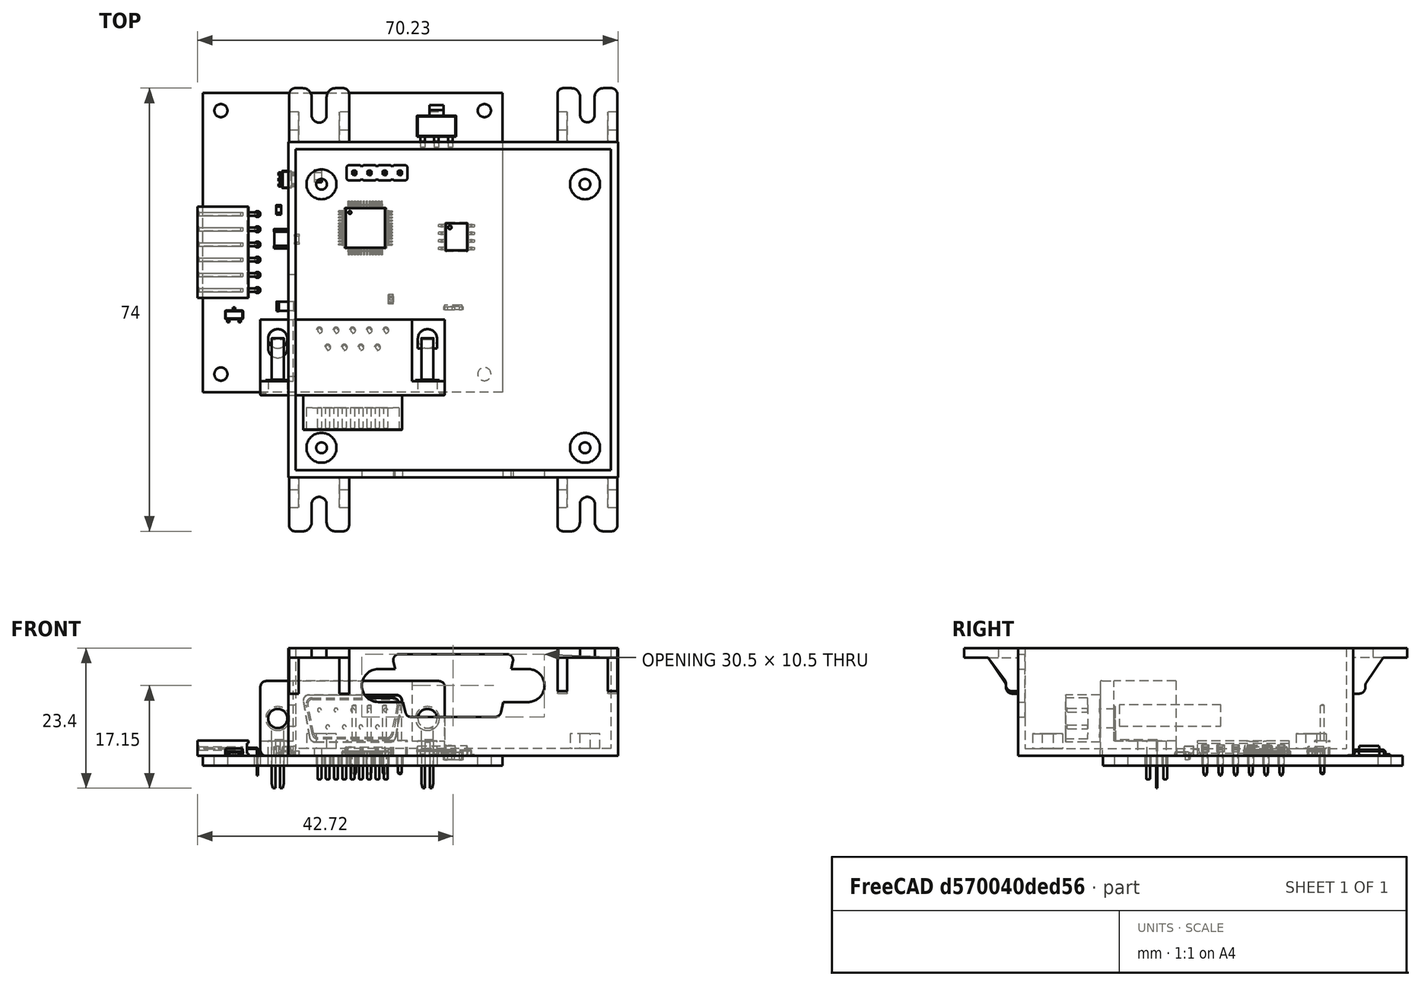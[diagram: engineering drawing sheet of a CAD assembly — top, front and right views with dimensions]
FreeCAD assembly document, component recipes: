
FREECAD ASSEMBLY — COMPONENT RECIPES ("CentralBox_Stuffed")

This assembly document has 6 components, labeled P0..P5 below (a component is one placed body or linked part). 5 of them carry a construction recipe — the FreeCAD feature program that regenerates the part from scratch, quoted from this document or its linked companion documents; the rest are supplied as boundary geometry only. No exploded tour is included for this assembly.
COMPONENT P0 — geometry summary ("CTB-01.kicad_pro"; no construction recipe available for this part):
  bounding box: 56.3 x 50.9 x 17.9 mm
  tessellated surface: 83,718 triangles
  volume: 7836 mm^3 (15% of its bounding box)
COMPONENT P1 — recipe-attached ("Body", modeled in this document).
Construction recipe (the document's own serialized feature program — sketch geometry with constraints, then the solid features built on it; lengths are millimeters unless a unit is written):

FEATURE [Sketcher::SketchObject] Sketch
  FullyConstrained = true
  MapMode = 2
  Support = -> [XY_Plane]
  expr: Constraints[8] = <<Params>>.box_width_external
  expr: Constraints[9] = <<Params>>.box_length_external
  sketch-geometry (4):
    g0: LineSegment StartX=-27.5 StartY=28 StartZ=0 EndX=27.5 EndY=28 EndZ=0
    g1: LineSegment StartX=27.5 StartY=28 StartZ=0 EndX=27.5 EndY=-28 EndZ=0
    g2: LineSegment StartX=27.5 StartY=-28 StartZ=0 EndX=-27.5 EndY=-28 EndZ=0
    g3: LineSegment StartX=-27.5 StartY=-28 StartZ=0 EndX=-27.5 EndY=28 EndZ=0
  constraints (10):
    c: Coincident(g0,g1)
    c: Coincident(g1,g2)
    c: Coincident(g2,g3)
    c: Coincident(g3,g0)
    c: Horizontal(g2)
    c: Vertical(g3)
    c: Symmetric(g0,g1,g-1)
    c: Symmetric(g0,g0,g-2)
    c: DistanceY(g2,g0) = 56
    c: DistanceX(g0,g0) = 55
FEATURE [PartDesign::Pad] Pad
  Direction = (0,0,1)
  Length = 18
  Length2 = 10
  Profile = -> Sketch
  ReferenceAxis = -> Sketch [N_Axis]
  Type = 0
  expr: Length = <<Params>>.box_height
FEATURE [Sketcher::SketchObject] Sketch012
  FullyConstrained = true
  MapMode = 5
  Placement = pos=(0,0,18) rot=(0,0,1;0rad)
  Support = -> [Pad]
  expr: Constraints[8] = <<Params>>.box_length_internal
  expr: Constraints[9] = <<Params>>.box_width_internal
  sketch-geometry (4):
    g0: LineSegment StartX=-26.3 StartY=26.8 StartZ=0 EndX=26.3 EndY=26.8 EndZ=0
    g1: LineSegment StartX=26.3 StartY=26.8 StartZ=0 EndX=26.3 EndY=-26.8 EndZ=0
    g2: LineSegment StartX=26.3 StartY=-26.8 StartZ=0 EndX=-26.3 EndY=-26.8 EndZ=0
    g3: LineSegment StartX=-26.3 StartY=-26.8 StartZ=0 EndX=-26.3 EndY=26.8 EndZ=0
  constraints (10):
    c: Coincident(g0,g1)
    c: Coincident(g1,g2)
    c: Coincident(g2,g3)
    c: Coincident(g3,g0)
    c: Horizontal(g2)
    c: Vertical(g1)
    c: Symmetric(g0,g0,g-2)
    c: Symmetric(g0,g2,g-1)
    c: DistanceX(g0,g0) = 52.6
    c: DistanceY(g2,g0) = 53.6
FEATURE [PartDesign::Pocket] Pocket
  BaseFeature = -> Pad
  Direction = (0,0,-1)
  Length = 16.8
  Length2 = 5
  Profile = -> Sketch012
  ReferenceAxis = -> Sketch012 [N_Axis]
  Type = 0
  expr: Length = <<Params>>.box_depth
FEATURE [PartDesign::SubShapeBinder] Binder
  BindCopyOnChange = 0
  BindMode = 0
  ClaimChildren = false
  Context = -> Body [Binder.]
  Fuse = false
  MakeFace = true
  OffsetFill = false
  OffsetIntersection = false
  OffsetJoinType = 0
  OffsetOpenResult = false
  PartialLoad = false
  Relative = true
  Support = -> [Board_1da8[Step_Models_1da8.Top_1da8.Shape011.Face27]]
  _Version = 2
FEATURE [Sketcher::SketchObject] Sketch013
  ExternalGeometry = -> [Binder]
  FullyConstrained = true
  MapMode = 5
  Placement = pos=(0,-28,0) rot=(1,0,0;1.5708rad)
  Support = -> [Pocket]
  sketch-geometry (17):
    g0: ArcOfCircle CenterX=12.49 CenterY=11.75 CenterZ=0 NormalX=0 NormalY=0 NormalZ=1 AngleXU=0 Radius=2.75 StartAngle=4.70512 EndAngle=7.85398
    g1: ArcOfCircle CenterX=-12.51 CenterY=11.75 CenterZ=0 NormalX=0 NormalY=0 NormalZ=1 AngleXU=0 Radius=2.75 StartAngle=1.5708 EndAngle=4.71239
    g2: LineSegment StartX=-12.51 StartY=9 StartZ=0 EndX=-8.39 EndY=9 EndZ=0
    g3: LineSegment StartX=-12.51 StartY=14.5 StartZ=0 EndX=-9.68 EndY=14.5 EndZ=0
    g4: LineSegment StartX=-12.51 StartY=11.75 StartZ=0 EndX=12.49 EndY=11.75 EndZ=0
    g5: ArcOfCircle CenterX=-9.01 CenterY=16 CenterZ=0 NormalX=0 NormalY=0 NormalZ=1 AngleXU=0 Radius=1 StartAngle=1.5708 EndAngle=3.37594
    g6: ArcOfCircle CenterX=8.99 CenterY=16 CenterZ=0 NormalX=0 NormalY=0 NormalZ=1 AngleXU=0 Radius=1 StartAngle=6.04884 EndAngle=7.85398
    g7: ArcOfCircle CenterX=6.99 CenterY=7.5 CenterZ=0 NormalX=0 NormalY=0 NormalZ=1 AngleXU=0 Radius=1 StartAngle=4.71239 EndAngle=6.06326
    g8: ArcOfCircle CenterX=-7.01 CenterY=7.5 CenterZ=0 NormalX=0 NormalY=0 NormalZ=1 AngleXU=0 Radius=1 StartAngle=3.37255 EndAngle=4.71239
    g9: LineSegment StartX=-9.01 StartY=17 StartZ=0 EndX=8.99 EndY=17 EndZ=0
    g10: LineSegment StartX=6.99 StartY=6.5 StartZ=0 EndX=-7.01 EndY=6.5 EndZ=0
    g11: LineSegment StartX=-7.98345 StartY=7.27109 StartZ=0 EndX=-8.39 EndY=9 EndZ=0
    g12: LineSegment StartX=7.96591 StartY=7.28184 StartZ=0 EndX=8.35 EndY=9 EndZ=0
    g13: LineSegment StartX=9.66 StartY=14.5 StartZ=0 EndX=12.49 EndY=14.5 EndZ=0
    g14: LineSegment StartX=-9.68 StartY=14.5 StartZ=0 EndX=-9.98267 EndY=15.7678 EndZ=0
    g15: LineSegment StartX=8.35 StartY=9 StartZ=0 EndX=12.47 EndY=9.00007 EndZ=0
    g16: LineSegment StartX=9.66 StartY=14.5 StartZ=0 EndX=9.96267 EndY=15.7678 EndZ=0
  constraints (44):
    c: Coincident(g0,g-4)
    c: Coincident(g1,g-3)
    c: Diameter(g1) = 5.5
    c: Equal(g1,g0)
    c: Coincident(g4,g1)
    c: Coincident(g4,g0)
    c: Diameter(g6) = 2
    c: Equal(g6,g5)
    c: Equal(g5,g8)
    c: Equal(g8,g7)
    c: Horizontal(g9)
    c: Horizontal(g10)
    c: DistanceY(g10,g9) = 10.5
    c: DistanceX(g5,g6) = 18
    c: DistanceX(g8,g7) = 14
    c: DistanceX(g7,g0) = 5.5
    c: DistanceY(g7,g0) = 4.25
    c: DistanceX(g6,g0) = 3.5
    c: Tangent(g5,g9) = 1.5708
    c: Tangent(g6,g9) = 1.5708
    c: Tangent(g7,g12) = -1.5708
    c: Tangent(g7,g10) = 1.5708
    c: Tangent(g8,g10) = 1.5708
    c: Tangent(g8,g11) = 1.5708
    c: Tangent(g1,g3) = 1.5708
    c: Tangent(g1,g2) = -1.5708
    c: Coincident(g0,g15) = -1.5708
    c: Coincident(g0,g13) = 1.5708
    c: Coincident(g14,g3)
    c: Coincident(g2,g11)
    c: Coincident(g16,g13)
    c: Coincident(g12,g15)
    c: Horizontal(g2,g12)
    c: Horizontal(g3,g13)
    c: Equal(g13,g3)
    c: Equal(g2,g15)
    c: DistanceX(g2,g2) = 4.12
    c: DistanceX(g1,g3) = 2.83
    c: DistanceY(g1,g3) = 2.75
    c: DistanceY(g2,g1) = 2.75
    c: DistanceX(g13,g0) = 2.83
    c: DistanceX(g12,g0) = 4.14
    c: Tangent(g5,g14) = 1.5708
    c: Tangent(g6,g16) = -1.5708
FEATURE [PartDesign::Pocket] Pocket001
  BaseFeature = -> Pocket
  Direction = (0,1,-2e-16)
  Length = 5
  Length2 = 5
  Profile = -> Sketch013
  ReferenceAxis = -> Sketch013 [N_Axis]
  Type = 2
FEATURE [Sketcher::SketchObject] Sketch014
  FullyConstrained = true
  MapMode = 5
  Placement = pos=(-27.5,0,0) rot=(0.57735,-0.57735,-0.57735;2.0944rad)
  Support = -> [Pocket001]
  expr: Constraints[10] = <<Params>>.side_window_height
  expr: Constraints[11] = <<Params>>.side_window_y
  expr: Constraints[8] = <<Params>>.side_window_length
  expr: Constraints[9] = <<Params>>.side_window_z
  sketch-geometry (4):
    g0: LineSegment StartX=-5.9 StartY=8.5 StartZ=0 EndX=11.1 EndY=8.5 EndZ=0
    g1: LineSegment StartX=11.1 StartY=8.5 StartZ=0 EndX=11.1 EndY=5 EndZ=0
    g2: LineSegment StartX=11.1 StartY=5 StartZ=0 EndX=-5.9 EndY=5 EndZ=0
    g3: LineSegment StartX=-5.9 StartY=5 StartZ=0 EndX=-5.9 EndY=8.5 EndZ=0
  constraints (12):
    c: Coincident(g0,g1)
    c: Coincident(g1,g2)
    c: Coincident(g2,g3)
    c: Coincident(g3,g0)
    c: Horizontal(g0)
    c: Horizontal(g2)
    c: Vertical(g1)
    c: Vertical(g3)
    c: DistanceX(g2,g1) = 17
    c: DistanceY(g-1,g2) = 5
    c: DistanceY(g2,g0) = 3.5
    c: DistanceX(g-1,g1) = 11.1
FEATURE [PartDesign::Pocket] Pocket002
  BaseFeature = -> Pocket001
  Direction = (1,0,0)
  Length = 5
  Length2 = 5
  Profile = -> Sketch014
  ReferenceAxis = -> Sketch014 [N_Axis]
  Type = 2
FEATURE [PartDesign::SubShapeBinder] Binder001
  BindCopyOnChange = 0
  BindMode = 0
  ClaimChildren = false
  Context = -> Body [Binder001.]
  Fuse = false
  MakeFace = true
  OffsetFill = false
  OffsetIntersection = false
  OffsetJoinType = 0
  OffsetOpenResult = false
  PartialLoad = false
  Relative = true
  Support = -> [Board_1da8[Board_Geoms_1da8.Pcb_1da8.]]
  _Version = 2
FEATURE [Sketcher::SketchObject] Sketch015
  ExternalGeometry = -> [Binder001]
  FullyConstrained = true
  MapMode = 5
  Placement = pos=(0,0,1.2) rot=(0,0,1;0rad)
  Support = -> [Pocket002]
  expr: Constraints[8] = <<Params>>.monting_boss_hole
  expr: Constraints[9] = <<Params>>.mounting_boss_pad
  sketch-geometry (8):
    g0: Circle CenterX=22 CenterY=-23.05 CenterZ=0 NormalX=0 NormalY=0 NormalZ=1 AngleXU=0 Radius=0.9
    g1: Circle CenterX=22 CenterY=-23.05 CenterZ=0 NormalX=0 NormalY=0 NormalZ=1 AngleXU=0 Radius=2.5
    g2: Circle CenterX=-22 CenterY=-23.05 CenterZ=0 NormalX=0 NormalY=0 NormalZ=1 AngleXU=0 Radius=0.9
    g3: Circle CenterX=-22 CenterY=-23.05 CenterZ=0 NormalX=0 NormalY=0 NormalZ=1 AngleXU=0 Radius=2.5
    g4: Circle CenterX=22 CenterY=20.95 CenterZ=0 NormalX=0 NormalY=0 NormalZ=1 AngleXU=0 Radius=0.9
    g5: Circle CenterX=22 CenterY=20.95 CenterZ=0 NormalX=0 NormalY=0 NormalZ=1 AngleXU=0 Radius=2.5
    g6: Circle CenterX=-22 CenterY=20.95 CenterZ=0 NormalX=0 NormalY=0 NormalZ=1 AngleXU=0 Radius=0.9
    g7: Circle CenterX=-22 CenterY=20.95 CenterZ=0 NormalX=0 NormalY=0 NormalZ=1 AngleXU=0 Radius=2.5
  constraints (16):
    c: Coincident(g0,g-5)
    c: Coincident(g1,g0)
    c: Coincident(g2,g-6)
    c: Coincident(g3,g2)
    c: Coincident(g4,g-4)
    c: Coincident(g5,g4)
    c: Coincident(g6,g-3)
    c: Coincident(g7,g6)
    c: Diameter(g4) = 1.8
    c: Diameter(g5) = 5
    c: Equal(g4,g2)
    c: Equal(g2,g0)
    c: Equal(g4,g6)
    c: Equal(g5,g7)
    c: Equal(g7,g1)
    c: Equal(g1,g3)
FEATURE [PartDesign::Pad] Pad010
  BaseFeature = -> Pocket002
  Direction = (0,0,1)
  Length = 2.5
  Length2 = 10
  Profile = -> Sketch015
  ReferenceAxis = -> Sketch015 [N_Axis]
  Type = 0
  expr: Length = <<Params>>.mounting_boss_height
FEATURE [PartDesign::Body] Body
  Group = -> [Sketch,Pad,Sketch012,Pocket,Binder,Sketch013,Pocket001,Sketch014,Pocket002,Binder001,Sketch015,Pad010]
  Origin = -> Origin
  Tip = -> Pad010
COMPONENT P2 — recipe-attached ("Tab1", modeled in this document).
Construction recipe (the document's own serialized feature program — sketch geometry with constraints, then the solid features built on it; lengths are millimeters unless a unit is written):

FEATURE [Sketcher::SketchObject] Sketch004
  FullyConstrained = true
  MapMode = 5
  Support = -> [XY_Plane009]
  expr: Constraints[13] = <<Params001>>.tab_length
  expr: Constraints[14] = <<Params001>>.tab_width
  expr: Constraints[19] = <<Params001>>.tab_hole_diameter
  expr: Constraints[20] = <<Params001>>.tab_hole_x
  sketch-geometry (8):
    g0: LineSegment StartX=-4.5 StartY=5 StartZ=0 EndX=4.5 EndY=5 EndZ=0
    g1: LineSegment StartX=4.5 StartY=5 StartZ=0 EndX=4.5 EndY=1.25 EndZ=0
    g2: LineSegment StartX=4.5 StartY=-5 StartZ=0 EndX=-4.5 EndY=-5 EndZ=0
    g3: LineSegment StartX=-4.5 StartY=-5 StartZ=0 EndX=-4.5 EndY=5 EndZ=0
    g4: ArcOfCircle CenterX=-1e-16 CenterY=0 CenterZ=0 NormalX=0 NormalY=0 NormalZ=1 AngleXU=0 Radius=1.25 StartAngle=1.5708 EndAngle=4.71239
    g5: LineSegment StartX=-3e-16 StartY=1.25 StartZ=0 EndX=4.5 EndY=1.25 EndZ=0
    g6: LineSegment StartX=4.5 StartY=-1.25 StartZ=0 EndX=0 EndY=-1.25 EndZ=0
    g7: LineSegment StartX=4.5 StartY=-1.25 StartZ=0 EndX=4.5 EndY=-5 EndZ=0
  constraints (21):
    c: Coincident(g0,g1)
    c: Coincident(g7,g2)
    c: Coincident(g2,g3)
    c: Coincident(g3,g0)
    c: Horizontal(g2)
    c: Vertical(g1)
    c: Symmetric(g0,g0,g-2)
    c: Symmetric(g0,g2,g-1)
    c: PointOnObject(g4,g-1)
    c: Horizontal(g5)
    c: Horizontal(g6)
    c: Coincident(g1,g5)
    c: Coincident(g7,g6)
    c: DistanceX(g0,g0) = 9
    c: DistanceY(g2,g0) = 10
    c: Tangent(g4,g5) = 1.5708
    c: Tangent(g6,g4) = 1.5708
    c: Vertical(g7)
    c: Vertical(g6,g1)
    c: Diameter(g4) = 2.5
    c: DistanceX(g0,g4) = 4.5
FEATURE [PartDesign::Pad] Pad002
  Direction = (0,0,1)
  Length = 1.6
  Length2 = 10
  Profile = -> Sketch004
  ReferenceAxis = -> Sketch004 [N_Axis]
  Type = 0
  expr: Length = <<Params001>>.tab_thickness
FEATURE [PartDesign::Plane] DatumPlane002  label="PlaneRib"
  Length = 60
  MapMode = 5
  Placement = pos=(0,-5,0) rot=(1,0,0;1.5708rad)
  ResizeMode = 0
  Support = -> [Pad002]
  Width = 60
FEATURE [Sketcher::SketchObject] Sketch005
  ExternalGeometry = -> [Pad002]
  FullyConstrained = true
  MapMode = 5
  Placement = pos=(0,-5,0) rot=(1,0,0;1.5708rad)
  Support = -> [DatumPlane002]
  expr: Constraints[11] = <<Params001>>.tab_rib_height
  expr: Constraints[12] = <<Params001>>.tab_rib_length
  expr: Constraints[13] = <<Params001>>.tab_rib_insert
  expr: Constraints[6] = <<Params001>>.tab_height
  sketch-geometry (5):
    g0: LineSegment StartX=-4.5 StartY=0 StartZ=0 EndX=-4.5 EndY=-5.6 EndZ=0
    g1: LineSegment StartX=-4.5 StartY=-5.6 StartZ=0 EndX=-2.5 EndY=-5.6 EndZ=0
    g2: LineSegment StartX=0.5 StartY=0 StartZ=0 EndX=-4.5 EndY=0 EndZ=0
    g3: LineSegment StartX=-2.5 StartY=-5.6 StartZ=0 EndX=-2.5 EndY=-4 EndZ=0
    g4: LineSegment StartX=-2.5 StartY=-4 StartZ=0 EndX=0.5 EndY=0 EndZ=0
  constraints (14):
    c: Coincident(g0,g-3)
    c: Vertical(g0)
    c: Coincident(g1,g0)
    c: PointOnObject(g2,g-1)
    c: Coincident(g2,g0)
    c: Horizontal(g1)
    c: DistanceY(g0,g0) = 5.6
    c: Coincident(g3,g1)
    c: Vertical(g3)
    c: Coincident(g4,g3)
    c: Coincident(g4,g2)
    c: DistanceY(g3,g-1) = 4
    c: DistanceX(g0,g2) = 5
    c: DistanceX(g0,g1) = 2
FEATURE [PartDesign::Pad] Pad003  label="TabRib1"
  BaseFeature = -> Pad002
  Direction = (0,-1,2e-16)
  Length = 1.6
  Length2 = 10
  Profile = -> Sketch005
  ReferenceAxis = -> Sketch005 [N_Axis]
  Reversed = true
  Type = 0
  expr: Length = <<Params001>>.tab_rib_thickness
FEATURE [PartDesign::LinearPattern] LinearPattern  label="TabRib2"
  BaseFeature = -> Pad003
  Direction = -> Y_Axis009
  Length = 8.4
  Occurrences = 2
  Originals = -> [Pad003]
  expr: Length = <<Params001>>.tab_ribs_gap
FEATURE [PartDesign::Fillet] Fillet
  Base = -> LinearPattern [Edge51,Edge52]
  BaseFeature = -> LinearPattern
  Radius = 1
  SupportTransform = false
  UseAllEdges = false
FEATURE [PartDesign::Fillet] Fillet001
  Base = -> Fillet [Edge14,Edge52]
  BaseFeature = -> Fillet
  Radius = 1
  SupportTransform = false
  UseAllEdges = false
FEATURE [PartDesign::Fillet] Fillet002
  Base = -> Fillet001 [Edge19,Edge53]
  BaseFeature = -> Fillet001
  Radius = 1
  SupportTransform = false
  UseAllEdges = false
FEATURE [PartDesign::Fillet] Fillet003
  Base = -> Fillet002 [Edge38,Edge43]
  BaseFeature = -> Fillet002
  Radius = 1.5
  SupportTransform = false
  UseAllEdges = false
FEATURE [PartDesign::Body] Body001  label="Tab1"
  Group = -> [Sketch004,Pad002,DatumPlane002,Sketch005,Pad003,LinearPattern,Fillet,Fillet001,Fillet002,Fillet003]
  Origin = -> Origin009
  Placement = pos=(22.4,-32.5,16.4) rot=(0,0,-1;1.5708rad)
  Tip = -> Fillet003
COMPONENT P3 — recipe-attached ("Tab2", modeled in this document).
Construction recipe (the document's own serialized feature program — sketch geometry with constraints, then the solid features built on it; lengths are millimeters unless a unit is written):

FEATURE [Sketcher::SketchObject] Sketch006
  FullyConstrained = true
  MapMode = 5
  Support = -> [XY_Plane010]
  expr: Constraints[13] = <<Params002>>.tab_length
  expr: Constraints[14] = <<Params002>>.tab_width
  expr: Constraints[19] = <<Params002>>.tab_hole_diameter
  expr: Constraints[20] = <<Params002>>.tab_hole_x
  sketch-geometry (8):
    g0: LineSegment StartX=-4.5 StartY=5 StartZ=0 EndX=4.5 EndY=5 EndZ=0
    g1: LineSegment StartX=4.5 StartY=5 StartZ=0 EndX=4.5 EndY=1.2 EndZ=0
    g2: LineSegment StartX=4.5 StartY=-5 StartZ=0 EndX=-4.5 EndY=-5 EndZ=0
    g3: LineSegment StartX=-4.5 StartY=-5 StartZ=0 EndX=-4.5 EndY=5 EndZ=0
    g4: ArcOfCircle CenterX=-3e-16 CenterY=0 CenterZ=0 NormalX=0 NormalY=0 NormalZ=1 AngleXU=0 Radius=1.2 StartAngle=1.5708 EndAngle=4.71239
    g5: LineSegment StartX=-5e-16 StartY=1.2 StartZ=0 EndX=4.5 EndY=1.2 EndZ=0
    g6: LineSegment StartX=4.5 StartY=-1.2 StartZ=0 EndX=-9e-16 EndY=-1.2 EndZ=0
    g7: LineSegment StartX=4.5 StartY=-1.2 StartZ=0 EndX=4.5 EndY=-5 EndZ=0
  constraints (21):
    c: Coincident(g0,g1)
    c: Coincident(g7,g2)
    c: Coincident(g2,g3)
    c: Coincident(g3,g0)
    c: Horizontal(g2)
    c: Vertical(g1)
    c: Symmetric(g0,g0,g-2)
    c: Symmetric(g0,g2,g-1)
    c: PointOnObject(g4,g-1)
    c: Horizontal(g5)
    c: Horizontal(g6)
    c: Coincident(g1,g5)
    c: Coincident(g7,g6)
    c: DistanceX(g0,g0) = 9
    c: DistanceY(g2,g0) = 10
    c: Tangent(g4,g5) = 1.5708
    c: Tangent(g6,g4) = 1.5708
    c: Vertical(g7)
    c: Vertical(g6,g1)
    c: Diameter(g4) = 2.4
    c: DistanceX(g0,g4) = 4.5
FEATURE [PartDesign::Pad] Pad004
  Direction = (0,0,1)
  Length = 1.6
  Length2 = 10
  Profile = -> Sketch006
  ReferenceAxis = -> Sketch006 [N_Axis]
  Type = 0
  expr: Length = <<Params002>>.tab_thickness
FEATURE [PartDesign::Plane] DatumPlane003  label="PlaneRib001"
  Length = 60
  MapMode = 5
  Placement = pos=(0,-5,0) rot=(1,0,0;1.5708rad)
  ResizeMode = 0
  Support = -> [Pad004]
  Width = 60
FEATURE [Sketcher::SketchObject] Sketch007
  ExternalGeometry = -> [Pad004]
  FullyConstrained = true
  MapMode = 5
  Placement = pos=(0,-5,0) rot=(1,0,0;1.5708rad)
  Support = -> [DatumPlane003]
  expr: Constraints[11] = <<Params002>>.tab_rib_height
  expr: Constraints[12] = <<Params002>>.tab_rib_length
  expr: Constraints[13] = <<Params002>>.tab_rib_insert
  expr: Constraints[6] = <<Params002>>.tab_height
  sketch-geometry (5):
    g0: LineSegment StartX=-4.5 StartY=0 StartZ=0 EndX=-4.5 EndY=-6 EndZ=0
    g1: LineSegment StartX=-4.5 StartY=-6 StartZ=0 EndX=-2.5 EndY=-6 EndZ=0
    g2: LineSegment StartX=0.5 StartY=0 StartZ=0 EndX=-4.5 EndY=0 EndZ=0
    g3: LineSegment StartX=-2.5 StartY=-6 StartZ=0 EndX=-2.5 EndY=-4.4 EndZ=0
    g4: LineSegment StartX=-2.5 StartY=-4.4 StartZ=0 EndX=0.5 EndY=0 EndZ=0
  constraints (14):
    c: Coincident(g0,g-3)
    c: Vertical(g0)
    c: Coincident(g1,g0)
    c: PointOnObject(g2,g-1)
    c: Coincident(g2,g0)
    c: Horizontal(g1)
    c: DistanceY(g0,g0) = 6
    c: Coincident(g3,g1)
    c: Vertical(g3)
    c: Coincident(g4,g3)
    c: Coincident(g4,g2)
    c: DistanceY(g3,g-1) = 4.4
    c: DistanceX(g0,g2) = 5
    c: DistanceX(g0,g1) = 2
FEATURE [PartDesign::Pad] Pad005  label="TabRib004"
  BaseFeature = -> Pad004
  Direction = (0,-1,2e-16)
  Length = 1.6
  Length2 = 10
  Profile = -> Sketch007
  ReferenceAxis = -> Sketch007 [N_Axis]
  Reversed = true
  Type = 0
  expr: Length = <<Params002>>.tab_rib_thickness
FEATURE [PartDesign::LinearPattern] LinearPattern001  label="TabRib003"
  BaseFeature = -> Pad005
  Direction = -> Y_Axis010
  Length = 8.4
  Occurrences = 2
  Originals = -> [Pad005]
  expr: Length = <<Params002>>.tab_ribs_gap
FEATURE [PartDesign::Fillet] Fillet004
  Base = -> LinearPattern001 [Edge51,Edge52]
  BaseFeature = -> LinearPattern001
  Radius = 1
  SupportTransform = false
  UseAllEdges = false
FEATURE [PartDesign::Fillet] Fillet005
  Base = -> Fillet004 [Edge14,Edge52]
  BaseFeature = -> Fillet004
  Radius = 1
  SupportTransform = false
  UseAllEdges = false
FEATURE [PartDesign::Fillet] Fillet006
  Base = -> Fillet005 [Edge19,Edge53]
  BaseFeature = -> Fillet005
  Radius = 1
  SupportTransform = false
  UseAllEdges = false
FEATURE [PartDesign::Fillet] Fillet007
  Base = -> Fillet006 [Edge38,Edge43]
  BaseFeature = -> Fillet006
  Radius = 1.5
  SupportTransform = false
  UseAllEdges = false
FEATURE [PartDesign::Body] Body002  label="Tab2"
  Group = -> [Sketch006,Pad004,DatumPlane003,Sketch007,Pad005,LinearPattern001,Fillet004,Fillet005,Fillet006,Fillet007]
  Origin = -> Origin010
  Placement = pos=(22.4,32.5,16.4) rot=(0,0,1;1.5708rad)
  Tip = -> Fillet007
COMPONENT P4 — recipe-attached ("Tab3", modeled in this document).
Construction recipe (the document's own serialized feature program — sketch geometry with constraints, then the solid features built on it; lengths are millimeters unless a unit is written):

FEATURE [Sketcher::SketchObject] Sketch008
  FullyConstrained = true
  MapMode = 5
  Support = -> [XY_Plane011]
  expr: Constraints[13] = <<Params003>>.tab_length
  expr: Constraints[14] = <<Params003>>.tab_width
  expr: Constraints[19] = <<Params003>>.tab_hole_diameter
  expr: Constraints[20] = <<Params003>>.tab_hole_x
  sketch-geometry (8):
    g0: LineSegment StartX=-4.5 StartY=5 StartZ=0 EndX=4.5 EndY=5 EndZ=0
    g1: LineSegment StartX=4.5 StartY=5 StartZ=0 EndX=4.5 EndY=1.25 EndZ=0
    g2: LineSegment StartX=4.5 StartY=-5 StartZ=0 EndX=-4.5 EndY=-5 EndZ=0
    g3: LineSegment StartX=-4.5 StartY=-5 StartZ=0 EndX=-4.5 EndY=5 EndZ=0
    g4: ArcOfCircle CenterX=-1e-16 CenterY=0 CenterZ=0 NormalX=0 NormalY=0 NormalZ=1 AngleXU=0 Radius=1.25 StartAngle=1.5708 EndAngle=4.71239
    g5: LineSegment StartX=-3e-16 StartY=1.25 StartZ=0 EndX=4.5 EndY=1.25 EndZ=0
    g6: LineSegment StartX=4.5 StartY=-1.25 StartZ=0 EndX=0 EndY=-1.25 EndZ=0
    g7: LineSegment StartX=4.5 StartY=-1.25 StartZ=0 EndX=4.5 EndY=-5 EndZ=0
  constraints (21):
    c: Coincident(g0,g1)
    c: Coincident(g7,g2)
    c: Coincident(g2,g3)
    c: Coincident(g3,g0)
    c: Horizontal(g2)
    c: Vertical(g1)
    c: Symmetric(g0,g0,g-2)
    c: Symmetric(g0,g2,g-1)
    c: PointOnObject(g4,g-1)
    c: Horizontal(g5)
    c: Horizontal(g6)
    c: Coincident(g1,g5)
    c: Coincident(g7,g6)
    c: DistanceX(g0,g0) = 9
    c: DistanceY(g2,g0) = 10
    c: Tangent(g4,g5) = 1.5708
    c: Tangent(g6,g4) = 1.5708
    c: Vertical(g7)
    c: Vertical(g6,g1)
    c: Diameter(g4) = 2.5
    c: DistanceX(g0,g4) = 4.5
FEATURE [PartDesign::Pad] Pad006
  Direction = (0,0,1)
  Length = 1.6
  Length2 = 10
  Profile = -> Sketch008
  ReferenceAxis = -> Sketch008 [N_Axis]
  Type = 0
  expr: Length = <<Params003>>.tab_thickness
FEATURE [PartDesign::Plane] DatumPlane004  label="PlaneRib002"
  Length = 60
  MapMode = 5
  Placement = pos=(0,-5,0) rot=(1,0,0;1.5708rad)
  ResizeMode = 0
  Support = -> [Pad006]
  Width = 60
FEATURE [Sketcher::SketchObject] Sketch009
  ExternalGeometry = -> [Pad006]
  FullyConstrained = true
  MapMode = 5
  Placement = pos=(0,-5,0) rot=(1,0,0;1.5708rad)
  Support = -> [DatumPlane004]
  expr: Constraints[11] = <<Params003>>.tab_rib_height
  expr: Constraints[12] = <<Params003>>.tab_rib_length
  expr: Constraints[13] = <<Params003>>.tab_rib_insert
  expr: Constraints[6] = <<Params003>>.tab_height
  sketch-geometry (5):
    g0: LineSegment StartX=-4.5 StartY=0 StartZ=0 EndX=-4.5 EndY=-6 EndZ=0
    g1: LineSegment StartX=-4.5 StartY=-6 StartZ=0 EndX=-2.5 EndY=-6 EndZ=0
    g2: LineSegment StartX=0.5 StartY=0 StartZ=0 EndX=-4.5 EndY=0 EndZ=0
    g3: LineSegment StartX=-2.5 StartY=-6 StartZ=0 EndX=-2.5 EndY=-4.4 EndZ=0
    g4: LineSegment StartX=-2.5 StartY=-4.4 StartZ=0 EndX=0.5 EndY=0 EndZ=0
  constraints (14):
    c: Coincident(g0,g-3)
    c: Vertical(g0)
    c: Coincident(g1,g0)
    c: PointOnObject(g2,g-1)
    c: Coincident(g2,g0)
    c: Horizontal(g1)
    c: DistanceY(g0,g0) = 6
    c: Coincident(g3,g1)
    c: Vertical(g3)
    c: Coincident(g4,g3)
    c: Coincident(g4,g2)
    c: DistanceY(g3,g-1) = 4.4
    c: DistanceX(g0,g2) = 5
    c: DistanceX(g0,g1) = 2
FEATURE [PartDesign::Pad] Pad007  label="TabRib006"
  BaseFeature = -> Pad006
  Direction = (0,-1,2e-16)
  Length = 1.6
  Length2 = 10
  Profile = -> Sketch009
  ReferenceAxis = -> Sketch009 [N_Axis]
  Reversed = true
  Type = 0
  expr: Length = <<Params003>>.tab_rib_thickness
FEATURE [PartDesign::LinearPattern] LinearPattern002  label="TabRib005"
  BaseFeature = -> Pad007
  Direction = -> Y_Axis011
  Length = 8.4
  Occurrences = 2
  Originals = -> [Pad007]
  expr: Length = <<Params003>>.tab_ribs_gap
FEATURE [PartDesign::Fillet] Fillet008
  Base = -> LinearPattern002 [Edge51,Edge52]
  BaseFeature = -> LinearPattern002
  Radius = 1
  SupportTransform = false
  UseAllEdges = false
FEATURE [PartDesign::Fillet] Fillet009
  Base = -> Fillet008 [Edge14,Edge52]
  BaseFeature = -> Fillet008
  Radius = 1
  SupportTransform = false
  UseAllEdges = false
FEATURE [PartDesign::Fillet] Fillet010
  Base = -> Fillet009 [Edge19,Edge53]
  BaseFeature = -> Fillet009
  Radius = 1
  SupportTransform = false
  UseAllEdges = false
FEATURE [PartDesign::Fillet] Fillet011
  Base = -> Fillet010 [Edge38,Edge43]
  BaseFeature = -> Fillet010
  Radius = 1.5
  SupportTransform = false
  UseAllEdges = false
FEATURE [PartDesign::Body] Body003  label="Tab3"
  Group = -> [Sketch008,Pad006,DatumPlane004,Sketch009,Pad007,LinearPattern002,Fillet008,Fillet009,Fillet010,Fillet011]
  Origin = -> Origin011
  Placement = pos=(-22.4,32.5,16.4) rot=(0,0,1;1.5708rad)
  Tip = -> Fillet011
COMPONENT P5 — recipe-attached ("Tab4", modeled in this document).
Construction recipe (the document's own serialized feature program — sketch geometry with constraints, then the solid features built on it; lengths are millimeters unless a unit is written):

FEATURE [Sketcher::SketchObject] Sketch010
  FullyConstrained = true
  MapMode = 5
  Support = -> [XY_Plane012]
  expr: Constraints[13] = <<Params004>>.tab_length
  expr: Constraints[14] = <<Params004>>.tab_width
  expr: Constraints[19] = <<Params004>>.tab_hole_diameter
  expr: Constraints[20] = <<Params004>>.tab_hole_x
  sketch-geometry (8):
    g0: LineSegment StartX=-4.5 StartY=5 StartZ=0 EndX=4.5 EndY=5 EndZ=0
    g1: LineSegment StartX=4.5 StartY=5 StartZ=0 EndX=4.5 EndY=1.25 EndZ=0
    g2: LineSegment StartX=4.5 StartY=-5 StartZ=0 EndX=-4.5 EndY=-5 EndZ=0
    g3: LineSegment StartX=-4.5 StartY=-5 StartZ=0 EndX=-4.5 EndY=5 EndZ=0
    g4: ArcOfCircle CenterX=-3e-16 CenterY=0 CenterZ=0 NormalX=0 NormalY=0 NormalZ=1 AngleXU=0 Radius=1.25 StartAngle=1.5708 EndAngle=4.71239
    g5: LineSegment StartX=-5e-16 StartY=1.25 StartZ=0 EndX=4.5 EndY=1.25 EndZ=0
    g6: LineSegment StartX=4.5 StartY=-1.25 StartZ=0 EndX=-9e-16 EndY=-1.25 EndZ=0
    g7: LineSegment StartX=4.5 StartY=-1.25 StartZ=0 EndX=4.5 EndY=-5 EndZ=0
  constraints (21):
    c: Coincident(g0,g1)
    c: Coincident(g7,g2)
    c: Coincident(g2,g3)
    c: Coincident(g3,g0)
    c: Horizontal(g2)
    c: Vertical(g1)
    c: Symmetric(g0,g0,g-2)
    c: Symmetric(g0,g2,g-1)
    c: PointOnObject(g4,g-1)
    c: Horizontal(g5)
    c: Horizontal(g6)
    c: Coincident(g1,g5)
    c: Coincident(g7,g6)
    c: DistanceX(g0,g0) = 9
    c: DistanceY(g2,g0) = 10
    c: Tangent(g4,g5) = 1.5708
    c: Tangent(g6,g4) = 1.5708
    c: Vertical(g7)
    c: Vertical(g6,g1)
    c: Diameter(g4) = 2.5
    c: DistanceX(g0,g4) = 4.5
FEATURE [PartDesign::Pad] Pad008
  Direction = (0,0,1)
  Length = 1.6
  Length2 = 10
  Profile = -> Sketch010
  ReferenceAxis = -> Sketch010 [N_Axis]
  Type = 0
  expr: Length = <<Params004>>.tab_thickness
FEATURE [PartDesign::Plane] DatumPlane005  label="PlaneRib003"
  Length = 60
  MapMode = 5
  Placement = pos=(0,-5,0) rot=(1,0,0;1.5708rad)
  ResizeMode = 0
  Support = -> [Pad008]
  Width = 60
FEATURE [Sketcher::SketchObject] Sketch011
  ExternalGeometry = -> [Pad008]
  FullyConstrained = true
  MapMode = 5
  Placement = pos=(0,-5,0) rot=(1,0,0;1.5708rad)
  Support = -> [DatumPlane005]
  expr: Constraints[11] = <<Params004>>.tab_rib_height
  expr: Constraints[12] = <<Params004>>.tab_rib_length
  expr: Constraints[13] = <<Params004>>.tab_rib_insert
  expr: Constraints[6] = <<Params004>>.tab_height
  sketch-geometry (5):
    g0: LineSegment StartX=-4.5 StartY=0 StartZ=0 EndX=-4.5 EndY=-6 EndZ=0
    g1: LineSegment StartX=-4.5 StartY=-6 StartZ=0 EndX=-2.5 EndY=-6 EndZ=0
    g2: LineSegment StartX=0.5 StartY=0 StartZ=0 EndX=-4.5 EndY=0 EndZ=0
    g3: LineSegment StartX=-2.5 StartY=-6 StartZ=0 EndX=-2.5 EndY=-4.4 EndZ=0
    g4: LineSegment StartX=-2.5 StartY=-4.4 StartZ=0 EndX=0.5 EndY=0 EndZ=0
  constraints (14):
    c: Coincident(g0,g-3)
    c: Vertical(g0)
    c: Coincident(g1,g0)
    c: PointOnObject(g2,g-1)
    c: Coincident(g2,g0)
    c: Horizontal(g1)
    c: DistanceY(g0,g0) = 6
    c: Coincident(g3,g1)
    c: Vertical(g3)
    c: Coincident(g4,g3)
    c: Coincident(g4,g2)
    c: DistanceY(g3,g-1) = 4.4
    c: DistanceX(g0,g2) = 5
    c: DistanceX(g0,g1) = 2
FEATURE [PartDesign::Pad] Pad009  label="TabRib008"
  BaseFeature = -> Pad008
  Direction = (0,-1,2e-16)
  Length = 1.6
  Length2 = 10
  Profile = -> Sketch011
  ReferenceAxis = -> Sketch011 [N_Axis]
  Reversed = true
  Type = 0
  expr: Length = <<Params004>>.tab_rib_thickness
FEATURE [PartDesign::LinearPattern] LinearPattern003  label="TabRib007"
  BaseFeature = -> Pad009
  Direction = -> Y_Axis012
  Length = 8.4
  Occurrences = 2
  Originals = -> [Pad009]
  expr: Length = <<Params004>>.tab_ribs_gap
FEATURE [PartDesign::Fillet] Fillet012
  Base = -> LinearPattern003 [Edge51,Edge52]
  BaseFeature = -> LinearPattern003
  Radius = 1
  SupportTransform = false
  UseAllEdges = false
FEATURE [PartDesign::Fillet] Fillet013
  Base = -> Fillet012 [Edge14,Edge52]
  BaseFeature = -> Fillet012
  Radius = 1
  SupportTransform = false
  UseAllEdges = false
FEATURE [PartDesign::Fillet] Fillet014
  Base = -> Fillet013 [Edge19,Edge53]
  BaseFeature = -> Fillet013
  Radius = 1
  SupportTransform = false
  UseAllEdges = false
FEATURE [PartDesign::Fillet] Fillet015
  Base = -> Fillet014 [Edge38,Edge43]
  BaseFeature = -> Fillet014
  Radius = 1.5
  SupportTransform = false
  UseAllEdges = false
FEATURE [PartDesign::Body] Body004  label="Tab4"
  Group = -> [Sketch010,Pad008,DatumPlane005,Sketch011,Pad009,LinearPattern003,Fillet012,Fillet013,Fillet014,Fillet015]
  Origin = -> Origin012
  Placement = pos=(-22.4,-32.5,16.4) rot=(0,0,-1;1.5708rad)
  Tip = -> Fillet015
PROVENANCE & LICENSES
A FreeCAD (.FCStd) document from a public repository crawl; recipes are the document's own serialized feature recipes (and, for linked parts, companion documents' recipes).
License: as declared in the source repository (recorded in the dataset sidecar).
